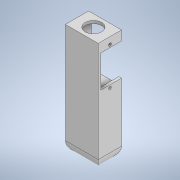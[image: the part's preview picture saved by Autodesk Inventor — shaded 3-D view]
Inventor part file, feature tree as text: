
AUTODESK INVENTOR PART (.ipt)
format: ipt  version: 2022.1 (Build 261234000, 234)  size: 202,752 bytes
history: native  units: mm
features: extrude x10, sketch x10, fillet x1
ambient origin geometry x8: Origin, YZ Plane, XZ Plane, XY Plane, X Axis, Y Axis, Z Axis, Center Point
bodies: Solid1 (feature_tree)
feature tree (21):
  extrude  "Extrusion1"  Depth=24.0mm
  extrude  "Extrusion2"  Depth=2.0mm
  extrude  "Extrusion3"  Depth=15.0mm TaperAngle=0.0deg
  extrude  "Extrusion4"  Depth=2.0mm
  extrude  "Extrusion5"  Depth=8.5mm
  extrude  "Extrusion6"  Depth=3.0mm
  extrude  "Extrusion7"  Depth=15.0mm
  extrude  "Extrusion8"  Depth=2.0mm
  extrude  "Extrusion9"  Depth=15.0mm TaperAngle=0.0deg
  fillet  "Fillet1"  Radius=5.0mm
  extrude  "Extrusion10"  Depth=2.0mm
  sketch  "Sketch1"  dims[d0=24.0mm d1=80.0mm]
  sketch  "Sketch2"  dims[d2=2.0mm d3=0.0mm d4=2.0mm]
  sketch  "Sketch3"  dims[d5=2.0mm d6=15.0mm d7=0.0mm]
  sketch  "Sketch4"  dims[d8=2.0mm d9=2.0mm]
  sketch  "Sketch5"  dims[d10=8.5mm d11=8.5mm]
  sketch  "Sketch6"  dims[d12=27.5mm d13=3.0mm]
  sketch  "Sketch7"  dims[d14=12.0mm d15=0.0mm d23=15.0mm]
  sketch  "Sketch8"  dims[d24=23.5mm d25=2.0mm]
  sketch  "Sketch9"  dims[d26=2.0mm d27=15.0mm d28=0.0mm d29=5.0mm]
  sketch  "Sketch10"  dims[d30=5.0mm d31=0.0mm d32=8.6mm d33=0.0mm d34=2.0mm d35=15.0mm d36=0.0mm d37=10.0mm d38=0.0mm d39=46.5mm d40=0.0mm d41=2.0mm d42=0.0mm d44=8.5mm d45=12.0mm d46=12.0mm d47=8.5mm d48=2.0mm d49=0.0mm]
